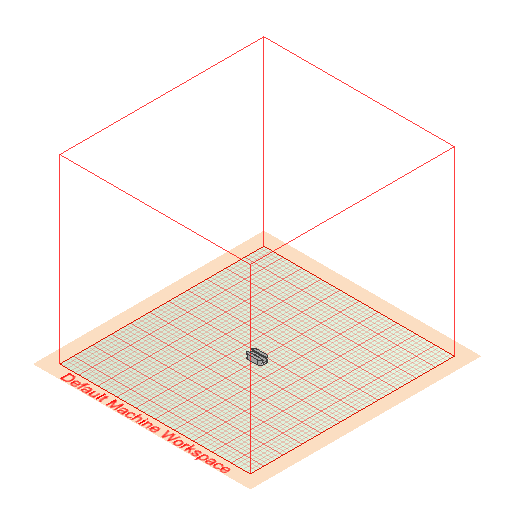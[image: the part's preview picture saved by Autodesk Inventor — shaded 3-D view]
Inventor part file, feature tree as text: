
AUTODESK INVENTOR PART (.ipt)
format: ipt  version: 2022 (Build 260153000, 153)  size: 498,176 bytes
history: native  units: mm
features: sketch x8, extrude x7, fillet x2, projected_geometry x2
ambient origin geometry x8: Origin, YZ Plane, XZ Plane, XY Plane, X Axis, Y Axis, Z Axis, Center Point
bodies: Solid1 (feature_tree)
feature tree (19):
  extrude  "Extrusion1"  Depth=9.0mm
  extrude  "Extrusion2"  Depth=35.0mm
  extrude  "Extrusion3"  Depth=5.0mm TaperAngle=0.0deg
  extrude  "Extrusion4"  Depth=6.0mm
  fillet  "Fillet1"  Radius=6.0mm
  fillet  "Fillet2"  Radius=3.0mm
  extrude  "Extrusion5"  Depth=7.0mm
  extrude  "Extrusion6"  Depth=6.0mm
  sketch  "Sketch7"  dims[d18=5.0mm d19=0.0mm d21=3.0mm]
  extrude  "Extrusion7"  Depth=3.0mm
  sketch  "Sketch1"  dims[d0=12.0mm d1=9.0mm]
  sketch  "Sketch2"  dims[d2=1.0mm d3=0.0mm d4=35.0mm]
  sketch  "Sketch3"  dims[d5=20.0mm d6=5.0mm d7=0.0mm]
  sketch  "Sketch4"  dims[d8=3.0mm d9=0.0mm d10=6.0mm d11=6.0mm d12=3.0mm d13=0.0mm]
  sketch  "Sketch5"  dims[d14=7.0mm d15=5.0mm]
  projected_geometry  "Projected Loop1"
  sketch  "Sketch6"  dims[d16=6.0mm d17=6.0mm]
  projected_geometry  "Projected Loop2"
  sketch  "Sketch8"  dims[d22=3.0mm d23=0.0mm d24=2.0mm d25=2.0mm d26=36.5mm d27=0.0mm d28=0.3mm d29=38.0mm d30=0.0mm d31=8.0mm]
